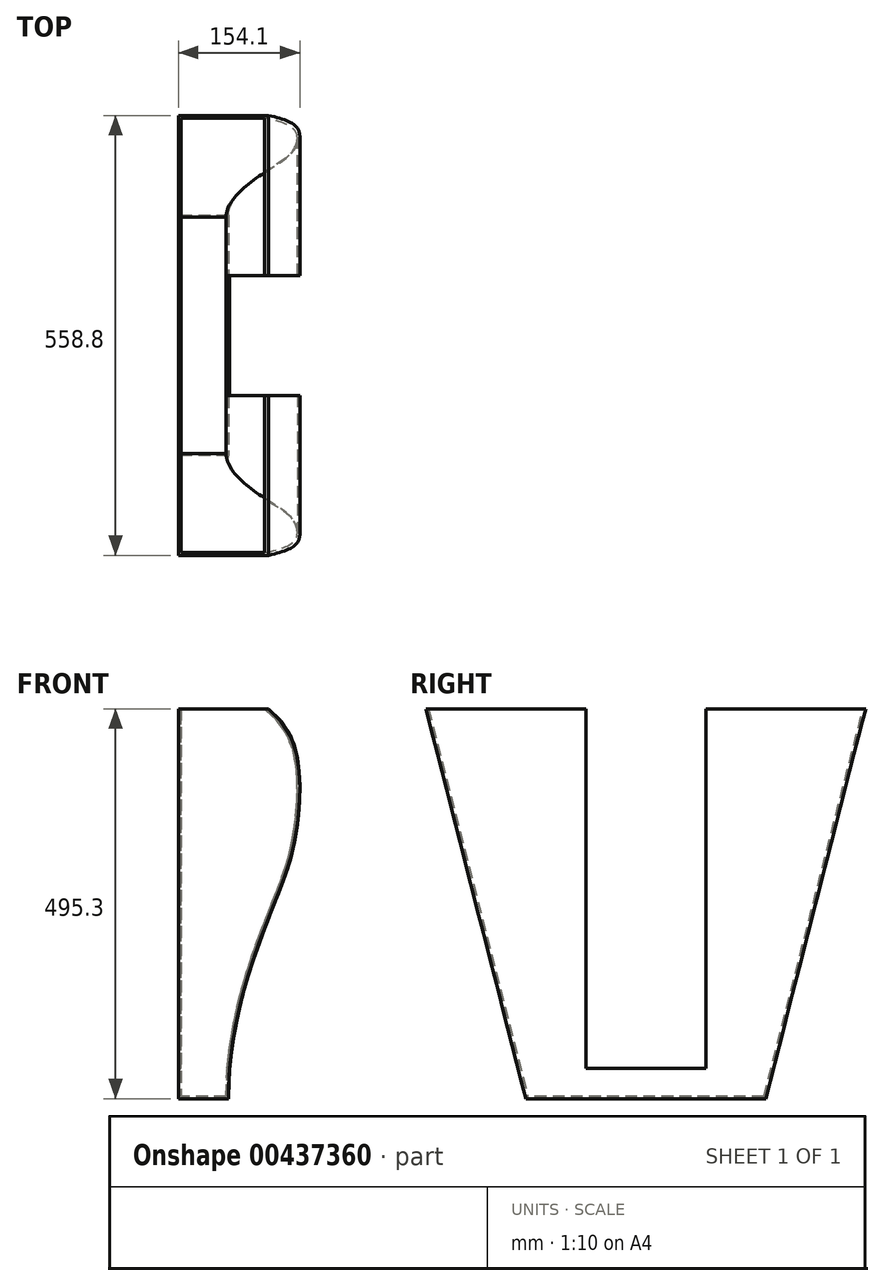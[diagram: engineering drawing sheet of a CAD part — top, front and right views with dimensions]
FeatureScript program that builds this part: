
annotation { "Feature Type Name" : "Feature", "Feature Type Description" : "" }
export const myFeature = defineFeature(function(context is Context, id is Id, definition is map)
    precondition{}
    {
        {
            var Q0;
            Q0=qCreatedBy(makeId("Top.planeOp"),FACE);
            var sketch = newSketch(context, id + "F0", { "sketchPlane" : qUnion([Q0])});
            skLineSegment(sketch, "E0.bottom", {"start": v(431.8, 381) * mm, "end": v(-431.8, 381) * mm});
            skLineSegment(sketch, "E0.top", {"start": v(431.8, -381) * mm, "end": v(-431.8, -381) * mm});
            skLineSegment(sketch, "E0.left", {"start": v(431.8, 381) * mm, "end": v(431.8, -381) * mm});
            skLineSegment(sketch, "E0.right", {"start": v(-431.8, 381) * mm, "end": v(-431.8, -381) * mm});
            skPoint(sketch, "E0.middle", {"position": v(0, 0) * mm});
            skLineSegment(sketch, "E1", {"start": v(-431.8, -381) * mm, "end": v(-431.8, -279.4) * mm});
            skLineSegment(sketch, "E2", {"start": v(-431.8, -279.4) * mm, "end": v(431.8, -279.4) * mm});
            skLineSegment(sketch, "E3", {"start": v(-431.8, 381) * mm, "end": v(-431.8, 279.4) * mm});
            skLineSegment(sketch, "E4", {"start": v(-431.8, 279.4) * mm, "end": v(431.8, 279.4) * mm});
            skLineSegment(sketch, "E5", {"start": v(-431.8, 279.4) * mm, "end": v(-431.8, -279.4) * mm});
            skLineSegment(sketch, "E6.bottom", {"start": v(431.8, 279.4) * mm, "end": v(-431.8, 279.4) * mm});
            skLineSegment(sketch, "E6.top", {"start": v(431.8, -279.4) * mm, "end": v(-431.8, -279.4) * mm});
            skLineSegment(sketch, "E6.left", {"start": v(431.8, 279.4) * mm, "end": v(431.8, -279.4) * mm});
            skLineSegment(sketch, "E7", {"start": v(431.8, 381) * mm, "end": v(431.8, 279.4) * mm});
            skLineSegment(sketch, "E8", {"start": v(431.8, -279.4) * mm, "end": v(431.8, -381) * mm});
            skSolve(sketch);
        }
        {
            var Q0;
            Q0=qCreatedBy(makeId("Top.planeOp"),FACE);
            cPlane(context, id + "F1", {"entities" : qUnion([Q0]), "cplaneType" : CPlaneType.OFFSET, "offset" : 114.3 * mm, "width" : 152.4 * mm, "height" : 152.4 * mm});
        }
        {
            var Q0;
            Q0=qCreatedBy(id+"F1.planeOp",FACE);
            cPlane(context, id + "F2", {"entities" : qUnion([Q0]), "cplaneType" : CPlaneType.OFFSET, "offset" : 495.3 * mm, "width" : 152.4 * mm, "height" : 152.4 * mm});
        }
        {
            var Q0;
            Q0=qCreatedBy(id+"F1.planeOp",FACE);
            var sketch = newSketch(context, id + "F3", { "sketchPlane" : qUnion([Q0])});
            skLineSegment(sketch, "E9", {"start": v(0, 0) * mm, "end": v(-400.05, 0) * mm, "construction": true});
            skLineSegment(sketch, "E10.bottom", {"start": v(-368.3, 152.4) * mm, "end": v(-431.8, 152.4) * mm});
            skLineSegment(sketch, "E10.top", {"start": v(-368.3, -152.4) * mm, "end": v(-431.8, -152.4) * mm});
            skLineSegment(sketch, "E10.left", {"start": v(-368.3, 152.4) * mm, "end": v(-368.3, -152.4) * mm});
            skLineSegment(sketch, "E10.right", {"start": v(-431.8, 152.4) * mm, "end": v(-431.8, -152.4) * mm});
            skPoint(sketch, "E10.middle", {"position": v(-400.05, 0) * mm});
            skSolve(sketch);
        }
        {
            var Q0;
            Q0=qCreatedBy(id+"F2.planeOp",FACE);
            var sketch = newSketch(context, id + "F4", { "sketchPlane" : qUnion([Q0])});
            skLineSegment(sketch, "E11", {"start": v(0, 0) * mm, "end": v(-304.8, 0) * mm, "construction": true});
            skLineSegment(sketch, "E12.bottom", {"start": v(-177.8, 279.4) * mm, "end": v(-431.8, 279.4) * mm});
            skLineSegment(sketch, "E12.top", {"start": v(-177.8, -279.4) * mm, "end": v(-431.8, -279.4) * mm});
            skLineSegment(sketch, "E12.left", {"start": v(-177.8, 279.4) * mm, "end": v(-177.8, -279.4) * mm});
            skLineSegment(sketch, "E12.right", {"start": v(-431.8, 279.4) * mm, "end": v(-431.8, -279.4) * mm});
            skPoint(sketch, "E12.middle", {"position": v(-304.8, 0) * mm});
            skSolve(sketch);
        }
        {
            var Q1;
            Q1 = qSketchRegion(id + "F3", true);
            var Q2;
            Q2 = qSketchRegion(id + "F4", true);
            loft(context, id + "F5", {"sheetProfilesArray" : [{ "sheetProfileEntities" : qUnion([Q1]) }, { "sheetProfileEntities" : qUnion([Q2]) }]});
        }
        {
            var Q0;
            Q0=qCreatedBy(makeId("Front.planeOp"),FACE);
            var sketch = newSketch(context, id + "F6", { "sketchPlane" : qUnion([Q0])});
            skLineSegment(sketch, "E13", {"start": v(0, 0) * mm, "end": v(0, 609.6) * mm, "construction": true});
            skLineSegment(sketch, "E14", {"start": v(0, 0) * mm, "end": v(-431.8, 0) * mm, "construction": true});
            skLineSegment(sketch, "E15", {"start": v(-431.8, 609.6) * mm, "end": v(-317.5, 609.6) * mm, "construction": true});
            skFitSpline(sketch, "E16", {"points": [v(-317.5, 609.6) * mm, v(-278.2, 524.8) * mm, v(-287.76, 426.24) * mm, v(-317.5, 343.1) * mm, v(-368.3, 114.3) * mm], "startDerivative": vector(407.9, -334.8) * mm, "endDerivative": vector(2.69, -804.33) * mm});
            skLineSegment(sketch, "E17", {"start": v(-431.8, 609.6) * mm, "end": v(-431.8, 114.3) * mm, "construction": true});
            skLineSegment(sketch, "E18", {"start": v(-431.8, 114.3) * mm, "end": v(-368.3, 114.3) * mm, "construction": true});
            skEllipse(sketch, "E19", {"center": v(-400.05, 114.3) * mm, "majorRadius": 31.75 * mm, "minorRadius": 4.17 * mm, "majorAxis": v(1, 0)});
            skLineSegment(sketch, "E20", {"start": v(-431.8, 609.6) * mm, "end": v(-431.8, 114.3) * mm});
            skLineSegment(sketch, "E21", {"start": v(-431.8, 609.6) * mm, "end": v(-317.5, 609.6) * mm});
            skLineSegment(sketch, "E22.bottom", {"start": v(-541.8, 701.62) * mm, "end": v(-169.9, 701.62) * mm});
            skLineSegment(sketch, "E22.top", {"start": v(-541.8, -48.07) * mm, "end": v(-169.9, -48.07) * mm});
            skLineSegment(sketch, "E22.left", {"start": v(-541.8, 701.62) * mm, "end": v(-541.8, -48.07) * mm});
            skLineSegment(sketch, "E22.right", {"start": v(-169.9, 701.62) * mm, "end": v(-169.9, -48.07) * mm});
            skSolve(sketch);
        }
        {
            var Q0;
            {var subQ2=sQuery(id+"F6.wireOp",EDGE,"E16");Q0=makeQuery(id+"F6.imprint","IMPRINT",FACE,{"disambiguationData":[TD([[makeQuery(id+"F6.imprint","IMPRINT",EDGE,{"derivedFrom":subQ2}),1.0]])]});}
            extrude(context, id + "F7", {"entities" : qUnion([Q0]), "operationType" : NewBodyOperationType.REMOVE, "endBound" : BoundingType.SYMMETRIC, "oppositeDirection" : true, "depth" : 1270 * mm});
        }
        {
            var Q0;
            Q0=makeQuery(id+"F5.opLoft","CAP_FACE",FACE,{"disambiguationData":[OSD([makeQuery(id+"F4.imprint","IMPRINT",FACE,{"disambiguationData":[TD([[makeQuery(id+"F4.imprint","IMPRINT",EDGE,{"derivedFrom":sQuery(id+"F4.wireOp",EDGE,"E12.bottom")}),1.0]])]})])],"isStart":true});
            shell(context, id + "F8", {"entities" : qUnion([Q0]), "thickness" : 3.17 * mm});
        }
        {
            var Q0;
            Q0=qCreatedBy(makeId("Right.planeOp"),FACE);
            var sketch = newSketch(context, id + "F9", { "sketchPlane" : qUnion([Q0])});
            skLineSegment(sketch, "E23.bottom", {"start": v(-76.2, 610.16) * mm, "end": v(76.2, 610.16) * mm});
            skLineSegment(sketch, "E23.top", {"start": v(-76.2, 152.96) * mm, "end": v(76.2, 152.96) * mm});
            skLineSegment(sketch, "E23.left", {"start": v(-76.2, 610.16) * mm, "end": v(-76.2, 152.96) * mm});
            skLineSegment(sketch, "E23.right", {"start": v(76.2, 610.16) * mm, "end": v(76.2, 152.96) * mm});
            skPoint(sketch, "E23.middle", {"position": v(0, 381.56) * mm});
            skSolve(sketch);
        }
        {
            var Q0;
            Q0 = qSketchRegion(id + "F9", true);
            extrude(context, id + "F10", {"entities" : qUnion([Q0]), "operationType" : NewBodyOperationType.REMOVE, "oppositeDirection" : true, "depth" : 609.6 * mm});
        }
    });
